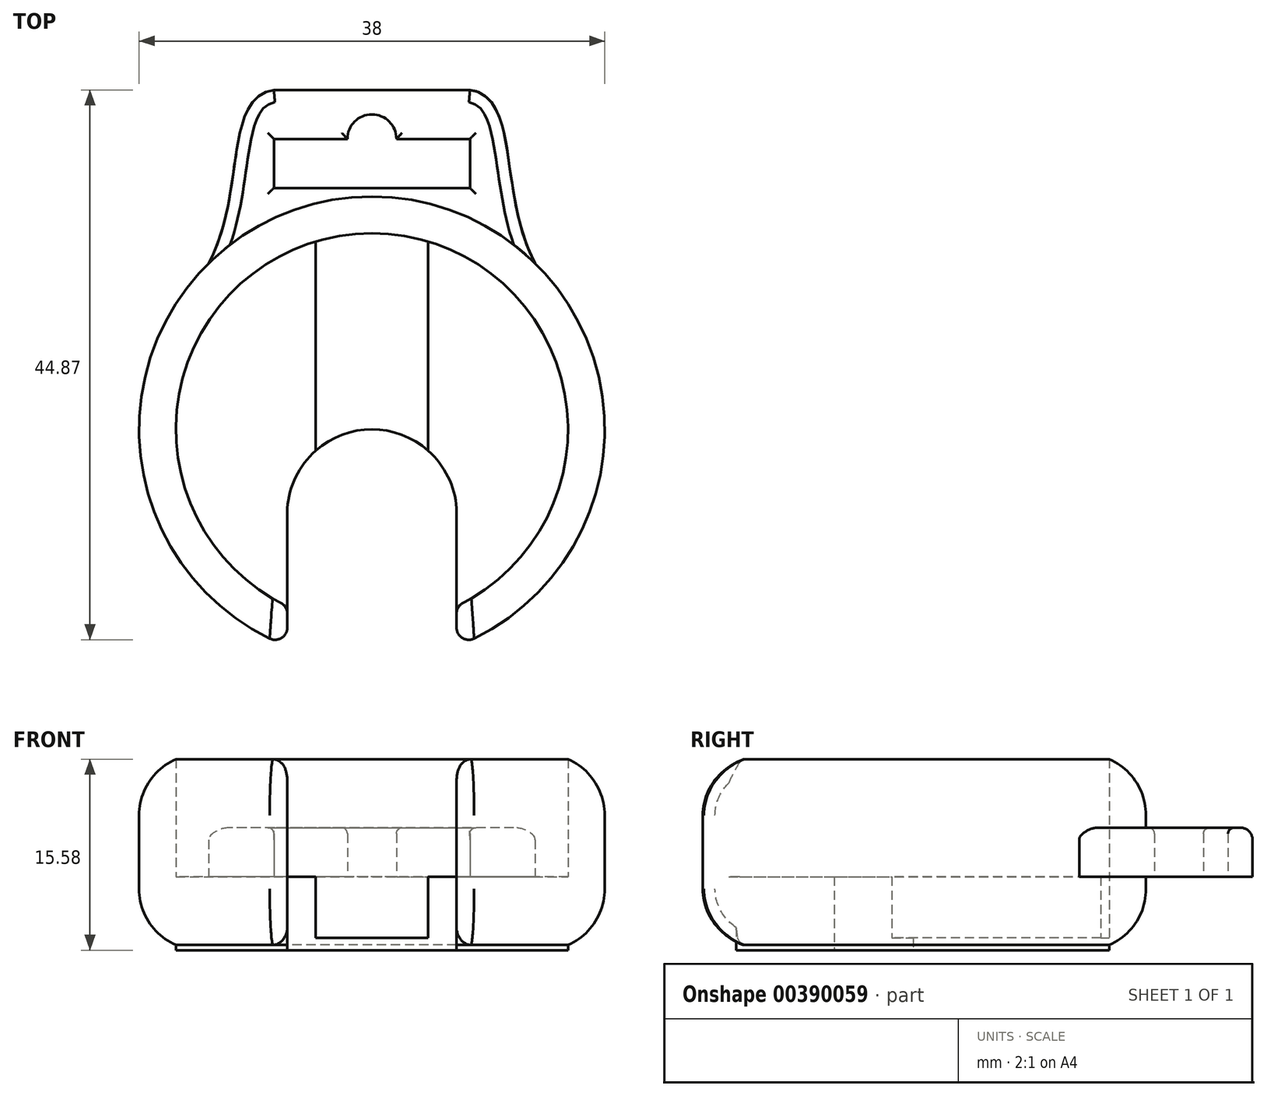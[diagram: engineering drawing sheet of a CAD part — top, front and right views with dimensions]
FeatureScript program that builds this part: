
annotation { "Feature Type Name" : "Feature", "Feature Type Description" : "" }
export const myFeature = defineFeature(function(context is Context, id is Id, definition is map)
    precondition{}
    {
        {
            var Q0;
            Q0=qCreatedBy(makeId("Top.planeOp"),FACE);
            var sketch = newSketch(context, id + "F0", { "sketchPlane" : qUnion([Q0])});
            skCircle(sketch, "E0", {"center": v(0, 0) * mm, "radius": 16 * mm});
            skCircle(sketch, "E1.0", {"center": v(0, 0) * mm, "radius": 19 * mm});
            skLineSegment(sketch, "E2.bottom", {"start": v(-4.6, 16) * mm, "end": v(4.6, 16) * mm});
            skLineSegment(sketch, "E2.top", {"start": v(-4.6, -16) * mm, "end": v(4.6, -16) * mm});
            skLineSegment(sketch, "E2.left", {"start": v(-4.6, 16) * mm, "end": v(-4.6, 15.32) * mm});
            skLineSegment(sketch, "E2.right", {"start": v(4.6, 16) * mm, "end": v(4.6, 15.32) * mm});
            skLineSegment(sketch, "E3", {"start": v(-4.6, 15.32) * mm, "end": v(-4.6, -15.32) * mm});
            skLineSegment(sketch, "E4", {"start": v(4.6, 15.32) * mm, "end": v(4.6, -15.32) * mm});
            skLineSegment(sketch, "E5", {"start": v(4.6, -15.32) * mm, "end": v(4.6, -16) * mm});
            skLineSegment(sketch, "E6", {"start": v(-4.6, -15.32) * mm, "end": v(-4.6, -16) * mm});
            skLineSegment(sketch, "E7", {"start": v(-15.4, -24.17) * mm, "end": v(15.4, -24.17) * mm});
            skPoint(sketch, "E8", {"position": v(0, -24.17) * mm});
            skSolve(sketch);
        }
        {
            var Q0;
            {var subQ3=sQuery(id+"F0.wireOp",EDGE,"E3");Q0=makeQuery(id+"F0.imprint","IMPRINT",FACE,{"disambiguationData":[TD([[makeQuery(id+"F0.imprint","IMPRINT",EDGE,{"derivedFrom":subQ3}),1.0]])]});}
            var Q1;
            {var subQ0=sQuery(id+"F0.wireOp",EDGE,"E6");Q1=makeQuery(id+"F0.imprint","IMPRINT",FACE,{"disambiguationData":[TD([[makeQuery(id+"F0.imprint","IMPRINT",EDGE,{"derivedFrom":subQ0}),1.0]])]});}
            var Q2;
            {var subQ0=sQuery(id+"F0.wireOp",EDGE,"E5");Q2=makeQuery(id+"F0.imprint","IMPRINT",FACE,{"disambiguationData":[TD([[makeQuery(id+"F0.imprint","IMPRINT",EDGE,{"derivedFrom":subQ0}),-1.0]])]});}
            extrude(context, id + "F1", {"entities" : qUnion([Q0, Q1, Q2]), "depth" : 1 * mm});
        }
        {
            var Q0;
            {var subQ0=sQuery(id+"F0.wireOp",EDGE,"E4");Q0=makeQuery(id+"F0.imprint","IMPRINT",FACE,{"disambiguationData":[TD([[makeQuery(id+"F0.imprint","IMPRINT",EDGE,{"derivedFrom":subQ0}),1.0]])]});}
            var Q1;
            {var subQ0=sQuery(id+"F0.wireOp",EDGE,"E3");Q1=makeQuery(id+"F0.imprint","IMPRINT",FACE,{"disambiguationData":[TD([[makeQuery(id+"F0.imprint","IMPRINT",EDGE,{"derivedFrom":subQ0}),-1.0]])]});}
            extrude(context, id + "F2", {"entities" : qUnion([Q0, Q1]), "operationType" : NewBodyOperationType.ADD, "depth" : 6 * mm});
        }
        {
            var Q0;
            {var subQ0=sQuery(id+"F0.wireOp",EDGE,"E2.left");Q0=makeQuery(id+"F0.imprint","IMPRINT",FACE,{"disambiguationData":[TD([[makeQuery(id+"F0.imprint","IMPRINT",EDGE,{"derivedFrom":subQ0}),1.0]])]});}
            var Q1;
            {var subQ0=sQuery(id+"F0.wireOp",EDGE,"E2.right");Q1=makeQuery(id+"F0.imprint","IMPRINT",FACE,{"disambiguationData":[TD([[makeQuery(id+"F0.imprint","IMPRINT",EDGE,{"derivedFrom":subQ0}),-1.0]])]});}
            var Q2;
            {var subQ0=sQuery(id+"F0.wireOp",EDGE,"E2.left");Q2=makeQuery(id+"F0.imprint","IMPRINT",FACE,{"disambiguationData":[TD([[makeQuery(id+"F0.imprint","IMPRINT",EDGE,{"derivedFrom":subQ0}),-1.0]])]});}
            extrude(context, id + "F3", {"entities" : qUnion([Q0, Q1, Q2]), "depth" : 16 * mm});
        }
        {
            var Q0;
            Q0=qCreatedBy(makeId("Top.planeOp"),FACE);
            cPlane(context, id + "F4", {"entities" : qUnion([Q0]), "cplaneType" : CPlaneType.OFFSET, "offset" : 8 * mm, "width" : 150 * mm, "height" : 150 * mm});
        }
        {
            var Q0;
            Q0=qCreatedBy(id+"F4.planeOp",FACE);
            var sketch = newSketch(context, id + "F5", { "sketchPlane" : qUnion([Q0])});
            skLineSegment(sketch, "E9.bottom", {"start": v(0, 27.7) * mm, "end": v(8, 27.7) * mm});
            skLineSegment(sketch, "E9.left", {"start": v(0, 27.7) * mm, "end": v(0, 25.7) * mm});
            skLineSegment(sketch, "E10.bottom", {"start": v(2, 23.7) * mm, "end": v(8, 23.7) * mm});
            skLineSegment(sketch, "E10.top", {"start": v(0, 19.7) * mm, "end": v(8, 19.7) * mm});
            skLineSegment(sketch, "E10.right", {"start": v(8, 23.7) * mm, "end": v(8, 19.7) * mm});
            skArc(sketch, "E11", {"start": v(0, 25.7) * mm, "mid": v(1.41, 25.11) * mm, "end": v(2, 23.7) * mm});
            skPoint(sketch, "E12.visualSharp", {"position": v(10, 27.7) * mm});
            skLineSegment(sketch, "E13.MirrorCS", {"start": v(0, 27.7) * mm, "end": v(-8, 27.7) * mm});
            skLineSegment(sketch, "E14.MirrorCS", {"start": v(0, 19.7) * mm, "end": v(-8, 19.7) * mm});
            skArc(sketch, "E15.MirrorCS", {"start": v(0, 25.7) * mm, "mid": v(-1.41, 25.11) * mm, "end": v(-2, 23.7) * mm});
            skLineSegment(sketch, "E16.MirrorCS", {"start": v(-2, 23.7) * mm, "end": v(-8, 23.7) * mm});
            skPoint(sketch, "E17.MirrorP", {"position": v(-10, 27.7) * mm});
            skLineSegment(sketch, "E18.MirrorCS", {"start": v(-8, 23.7) * mm, "end": v(-8, 19.7) * mm});
            skLineSegment(sketch, "E19", {"start": v(-21.59, 10.52) * mm, "end": v(-12.05, 10.52) * mm});
            skFitSpline(sketch, "E20", {"points": [v(-8, 27.7) * mm, v(-15.68, 10.52) * mm], "startDerivative": vector(-14.86, -2.26) * mm, "endDerivative": vector(-19.14, -16.92) * mm});
            skFitSpline(sketch, "E21.MirrorCS", {"points": [v(8, 27.7) * mm, v(15.68, 10.52) * mm], "startDerivative": vector(14.86, -2.26) * mm, "endDerivative": vector(19.14, -16.92) * mm});
            skArc(sketch, "E22", {"start": v(-12.05, 10.52) * mm, "mid": v(0, 16) * mm, "end": v(12.05, 10.52) * mm});
            skLineSegment(sketch, "E23.trimOffspring", {"start": v(12.05, 10.52) * mm, "end": v(25.78, 10.52) * mm});
            skSolve(sketch);
        }
        {
            var Q0;
            Q0=makeQuery(id+"F3.opExtrude","CAP_EDGE",EDGE,{"disambiguationData":[OSD([sQuery(id+"F0.wireOp",EDGE,"E1.0")])],"isStart":false});
            fillet(context, id + "F6", {"entities" : qUnion([Q0]), "radius" : 5 * mm, "tangentPropagation" : true, "allowEdgeOverflow" : false});
        }
        {
            var Q0;
            Q0=makeQuery(id+"F3.opExtrude","CAP_EDGE",EDGE,{"disambiguationData":[OSD([sQuery(id+"F0.wireOp",EDGE,"E1.0")])],"isStart":true});
            fillet(context, id + "F7", {"entities" : qUnion([Q0]), "radius" : 5 * mm, "tangentPropagation" : true, "allowEdgeOverflow" : false});
        }
        {
            var Q0;
            Q0=makeQuery(id+"F5.imprint","IMPRINT",FACE,{"disambiguationData":[TD([[makeQuery(id+"F5.imprint","IMPRINT",EDGE,{"derivedFrom":sQuery(id+"F5.wireOp",EDGE,"E9.bottom")}),-1.0]])]});
            extrude(context, id + "F8", {"entities" : qUnion([Q0]), "operationType" : NewBodyOperationType.ADD, "endBound" : BoundingType.SYMMETRIC, "depth" : 4 * mm});
        }
        {
            var Q0;
            Q0=makeQuery(id+"F8.opExtrude","CAP_EDGE",EDGE,{"disambiguationData":[OSD([sQuery(id+"F5.wireOp",EDGE,"E9.bottom"),sQuery(id+"F5.wireOp",EDGE,"E13.MirrorCS")])],"isStart":false});
            var Q1;
            Q1=makeQuery(id+"F8.opExtrude","CAP_EDGE",EDGE,{"disambiguationData":[OSD([sQuery(id+"F5.wireOp",EDGE,"E21.MirrorCS")])],"isStart":false});
            var Q2;
            Q2=makeQuery(id+"F8.opExtrude","CAP_EDGE",EDGE,{"disambiguationData":[OSD([sQuery(id+"F5.wireOp",EDGE,"E20")])],"isStart":false});
            fillet(context, id + "F9", {"entities" : qUnion([Q0, Q1, Q2]), "radius" : 1 * mm, "tangentPropagation" : true, "allowEdgeOverflow" : false});
        }
        {
            var Q0;
            Q0=makeQuery(id+"F8.opExtrude","CAP_EDGE",EDGE,{"disambiguationData":[OSD([sQuery(id+"F5.wireOp",EDGE,"E10.top"),sQuery(id+"F5.wireOp",EDGE,"E14.MirrorCS")])],"isStart":false});
            var Q1;
            Q1=makeQuery(id+"F8.opExtrude","CAP_EDGE",EDGE,{"disambiguationData":[OSD([sQuery(id+"F5.wireOp",EDGE,"E10.right")])],"isStart":false});
            var Q2;
            Q2=makeQuery(id+"F8.opExtrude","CAP_EDGE",EDGE,{"disambiguationData":[OSD([sQuery(id+"F5.wireOp",EDGE,"E10.bottom")])],"isStart":false});
            var Q3;
            Q3=makeQuery(id+"F8.opExtrude","CAP_EDGE",EDGE,{"disambiguationData":[OSD([sQuery(id+"F5.wireOp",EDGE,"E11"),sQuery(id+"F5.wireOp",EDGE,"E15.MirrorCS")])],"isStart":false});
            var Q4;
            Q4=makeQuery(id+"F8.opExtrude","CAP_EDGE",EDGE,{"disambiguationData":[OSD([sQuery(id+"F5.wireOp",EDGE,"E16.MirrorCS")])],"isStart":false});
            var Q5;
            Q5=makeQuery(id+"F8.opExtrude","CAP_EDGE",EDGE,{"disambiguationData":[OSD([sQuery(id+"F5.wireOp",EDGE,"E18.MirrorCS")])],"isStart":false});
            fillet(context, id + "F10", {"entities" : qUnion([Q0, Q1, Q2, Q3, Q4, Q5]), "radius" : 0.5 * mm, "tangentPropagation" : true, "allowEdgeOverflow" : false});
        }
        {
            var Q0;
            Q0=qCreatedBy(makeId("Top.planeOp"),FACE);
            var sketch = newSketch(context, id + "F11", { "sketchPlane" : qUnion([Q0])});
            skLineSegment(sketch, "E24.top", {"start": v(-6.9, -32.76) * mm, "end": v(6.9, -32.76) * mm});
            skLineSegment(sketch, "E24.left", {"start": v(-6.9, -6.44) * mm, "end": v(-6.9, -32.76) * mm});
            skLineSegment(sketch, "E24.right", {"start": v(6.9, -6.44) * mm, "end": v(6.9, -32.76) * mm});
            skPoint(sketch, "E24.middle", {"position": v(0, -19.6) * mm});
            skArc(sketch, "E25", {"start": v(6.9, -6.44) * mm, "mid": v(0, 0) * mm, "end": v(-6.9, -6.44) * mm});
            skSolve(sketch);
        }
        {
            var Q0;
            Q0=makeQuery(id+"F11.imprint","IMPRINT",FACE,{"disambiguationData":[TD([[makeQuery(id+"F11.imprint","IMPRINT",EDGE,{"derivedFrom":sQuery(id+"F11.wireOp",EDGE,"E24.top")}),1.0]])]});
            extrude(context, id + "F12", {"entities" : qUnion([Q0]), "operationType" : NewBodyOperationType.REMOVE, "endBound" : BoundingType.THROUGH_ALL, "depth" : 25 * mm});
        }
        {
            var Q0;
            Q0=makeQuery(id+"F12.boolean.opBoolean","INTERSECT",EDGE,{"derivedFrom":[makeQuery(id+"F3.opExtrude","SWEPT_FACE",FACE,{"disambiguationData":[OSD([sQuery(id+"F0.wireOp",EDGE,"E1.0")])]}),makeQuery(id+"F12.opExtrude","SWEPT_FACE",FACE,{"disambiguationData":[OSD([sQuery(id+"F11.wireOp",EDGE,"E24.right")])]})]});
            var Q1;
            Q1=makeQuery(id+"F12.boolean.opBoolean","INTERSECT",EDGE,{"derivedFrom":[makeQuery(id+"F6.opFillet","BLEND_FACE",FACE,{"disambiguationData":[OSD([sQuery(id+"F0.wireOp",EDGE,"E1.0")])]}),makeQuery(id+"F12.opExtrude","SWEPT_FACE",FACE,{"disambiguationData":[OSD([sQuery(id+"F11.wireOp",EDGE,"E24.left")])]})]});
            var Q2;
            Q2=makeQuery(id+"F12.boolean.opBoolean","INTERSECT",EDGE,{"derivedFrom":[makeQuery(id+"F3.opExtrude","SWEPT_FACE",FACE,{"disambiguationData":[OSD([sQuery(id+"F0.wireOp",EDGE,"E0")])]}),makeQuery(id+"F12.opExtrude","SWEPT_FACE",FACE,{"disambiguationData":[OSD([sQuery(id+"F11.wireOp",EDGE,"E24.left")])]})]});
            var Q3;
            Q3=makeQuery(id+"F12.boolean.opBoolean","INTERSECT",EDGE,{"derivedFrom":[makeQuery(id+"F3.opExtrude","SWEPT_FACE",FACE,{"disambiguationData":[OSD([sQuery(id+"F0.wireOp",EDGE,"E0")])]}),makeQuery(id+"F12.opExtrude","SWEPT_FACE",FACE,{"disambiguationData":[OSD([sQuery(id+"F11.wireOp",EDGE,"E24.right")])]})]});
            fillet(context, id + "F13", {"entities" : qUnion([Q0, Q1, Q2, Q3]), "radius" : 1 * mm, "tangentPropagation" : true, "allowEdgeOverflow" : false});
        }
    });
